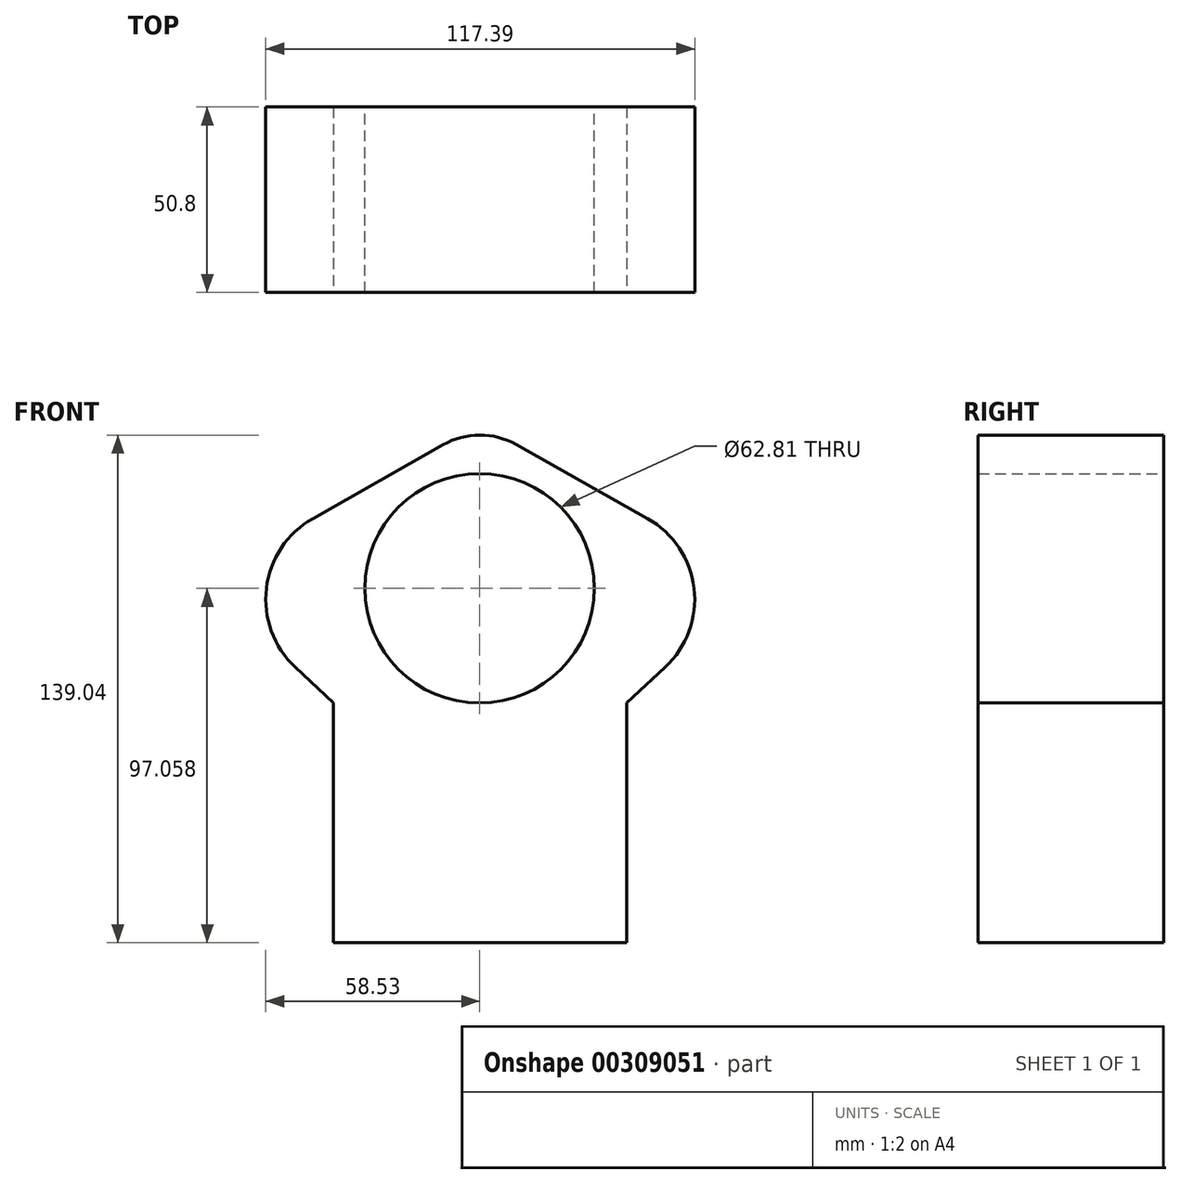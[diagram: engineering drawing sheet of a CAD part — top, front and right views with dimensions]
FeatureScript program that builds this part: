
annotation { "Feature Type Name" : "Feature", "Feature Type Description" : "" }
export const myFeature = defineFeature(function(context is Context, id is Id, definition is map)
    precondition{}
    {
        {
            var Q0;
            Q0=qCreatedBy(makeId("Front.planeOp"),FACE);
            var sketch = newSketch(context, id + "F0", { "sketchPlane" : qUnion([Q0])});
            skLineSegment(sketch, "E0", {"start": v(40.28, -65.72) * mm, "end": v(40.28, 0) * mm});
            skLineSegment(sketch, "E1", {"start": v(40.28, 0) * mm, "end": v(76.22, 33.4) * mm});
            skLineSegment(sketch, "E2", {"start": v(76.22, 33.4) * mm, "end": v(0, 76.34) * mm});
            skLineSegment(sketch, "E3", {"start": v(0, 76.34) * mm, "end": v(-75.76, 33.4) * mm});
            skLineSegment(sketch, "E4", {"start": v(-75.76, 33.4) * mm, "end": v(-39.97, 0) * mm});
            skLineSegment(sketch, "E5", {"start": v(-39.97, 0) * mm, "end": v(-39.97, -65.72) * mm});
            skLineSegment(sketch, "E6", {"start": v(-39.97, -65.72) * mm, "end": v(40.28, -65.72) * mm});
            skSolve(sketch);
        }
        {
            var Q0;
            Q0=makeQuery(id+"F0.imprint","IMPRINT",FACE,{"disambiguationData":[TD([[makeQuery(id+"F0.imprint","IMPRINT",EDGE,{"derivedFrom":sQuery(id+"F0.wireOp",EDGE,"E0")}),1.0]])]});
            extrude(context, id + "F1", {"entities" : qUnion([Q0]), "oppositeDirection" : true, "depth" : 50.8 * mm});
        }
        {
            var Q0;
            Q0=makeQuery(id+"F1.opExtrude","SWEPT_EDGE",EDGE,{"disambiguationData":[OSD([sQuery(id+"F0.wireOp",EDGE,"E2"),sQuery(id+"F0.wireOp",EDGE,"E3")])]});
            fillet(context, id + "F2", {"entities" : qUnion([Q0]), "radius" : 20.32 * mm, "tangentPropagation" : true, "allowEdgeOverflow" : false});
        }
        {
            var Q0;
            Q0=makeQuery(id+"F1.opExtrude","SWEPT_EDGE",EDGE,{"disambiguationData":[OSD([sQuery(id+"F0.wireOp",EDGE,"E1"),sQuery(id+"F0.wireOp",EDGE,"E2")])]});
            fillet(context, id + "F3", {"entities" : qUnion([Q0]), "radius" : 25.4 * mm, "tangentPropagation" : true, "allowEdgeOverflow" : false});
        }
        {
            var Q0;
            Q0=makeQuery(id+"F1.opExtrude","SWEPT_EDGE",EDGE,{"disambiguationData":[OSD([sQuery(id+"F0.wireOp",EDGE,"E3"),sQuery(id+"F0.wireOp",EDGE,"E4")])]});
            fillet(context, id + "F4", {"entities" : qUnion([Q0]), "radius" : 25.4 * mm, "tangentPropagation" : true, "allowEdgeOverflow" : false});
        }
        {
            var Q0;
            Q0=makeQuery(id+"F1.opExtrude","CAP_FACE",FACE,{"disambiguationData":[OSD([sQuery(id+"F0.wireOp",EDGE,"E0"),sQuery(id+"F0.wireOp",EDGE,"E1"),sQuery(id+"F0.wireOp",EDGE,"E2"),sQuery(id+"F0.wireOp",EDGE,"E3"),sQuery(id+"F0.wireOp",EDGE,"E4"),sQuery(id+"F0.wireOp",EDGE,"E5"),sQuery(id+"F0.wireOp",EDGE,"E6")])],"isStart":false});
            var sketch = newSketch(context, id + "F5", { "sketchPlane" : qUnion([Q0])});
            skCircle(sketch, "E7", {"center": v(0, 31.34) * mm, "radius": 31.4 * mm});
            skPoint(sketch, "E7.centerSnap0", {"position": v(58.36, 31.34) * mm});
            skSolve(sketch);
        }
        {
            var Q0;
            Q0=makeQuery(id+"F5.imprint","IMPRINT",FACE,{"disambiguationData":[TD([[makeQuery(id+"F5.imprint","IMPRINT",EDGE,{"derivedFrom":sQuery(id+"F5.wireOp",EDGE,"E7")}),1.0]])]});
            extrude(context, id + "F6", {"entities" : qUnion([Q0]), "operationType" : NewBodyOperationType.REMOVE, "endBound" : BoundingType.THROUGH_ALL, "oppositeDirection" : true, "depth" : 25.4 * mm});
        }
    });
